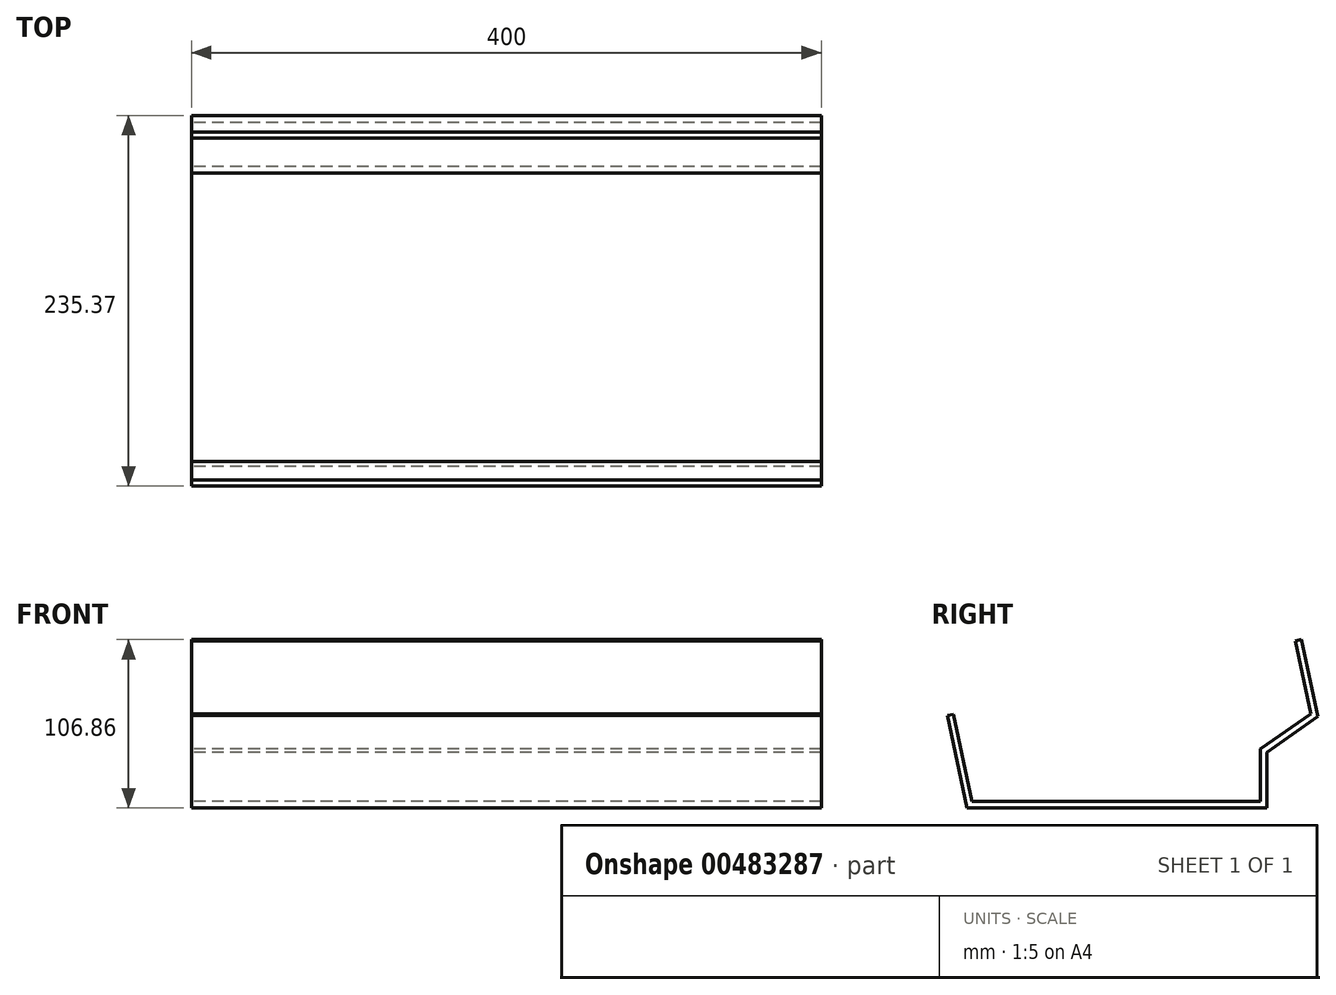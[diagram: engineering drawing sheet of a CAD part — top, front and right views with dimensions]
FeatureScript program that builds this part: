
annotation { "Feature Type Name" : "Feature", "Feature Type Description" : "" }
export const myFeature = defineFeature(function(context is Context, id is Id, definition is map)
    precondition{}
    {
        {
            var Q0;
            Q0=qCreatedBy(makeId("Right.planeOp"),FACE);
            var sketch = newSketch(context, id + "F0", { "sketchPlane" : qUnion([Q0])});
            skLineSegment(sketch, "E0", {"start": v(-66.5, 0) * mm, "end": v(158.4, 48.19) * mm});
            skLineSegment(sketch, "E1", {"start": v(-66.5, 0) * mm, "end": v(-53.93, -58.67) * mm});
            skLineSegment(sketch, "E2", {"start": v(-53.93, -58.67) * mm, "end": v(136.35, -58.67) * mm});
            skLineSegment(sketch, "E3", {"start": v(158.4, 48.19) * mm, "end": v(168.87, -0.7) * mm});
            skLineSegment(sketch, "E4", {"start": v(136.35, -23.34) * mm, "end": v(136.35, -58.67) * mm});
            skLineSegment(sketch, "E5", {"start": v(136.35, -23.34) * mm, "end": v(168.87, -0.7) * mm});
            skLineSegment(sketch, "E6.0", {"start": v(154.48, 47.35) * mm, "end": v(164.4, 1.06) * mm});
            skLineSegment(sketch, "E6.1", {"start": v(-62.6, 0.84) * mm, "end": v(-50.7, -54.67) * mm});
            skLineSegment(sketch, "E6.2", {"start": v(-50.7, -54.67) * mm, "end": v(132.35, -54.67) * mm});
            skLineSegment(sketch, "E6.3", {"start": v(132.35, -21.25) * mm, "end": v(132.35, -54.67) * mm});
            skLineSegment(sketch, "E6.4", {"start": v(132.35, -21.25) * mm, "end": v(164.4, 1.06) * mm});
            skSolve(sketch);
        }
        {
            var Q0;
            Q0=makeQuery(id+"F0.imprint","IMPRINT",FACE,{"disambiguationData":[TD([[makeQuery(id+"F0.imprint","IMPRINT",EDGE,{"derivedFrom":sQuery(id+"F0.wireOp",EDGE,"vrPzw0TB-PHxg-kVzE-N9qx-DRdmJ4r2id8z.bottom")}),1.0]])]});
            var Q1;
            Q1=makeQuery(id+"F0.imprint","IMPRINT",FACE,{"disambiguationData":[TD([[makeQuery(id+"F0.imprint","IMPRINT",EDGE,{"derivedFrom":sQuery(id+"F0.wireOp",EDGE,"E0")}),-1.0]])]});
            extrude(context, id + "F1", {"entities" : qUnion([Q0, Q1]), "depth" : 400 * mm, "offsetDistance" : 25 * mm});
        }
    });
